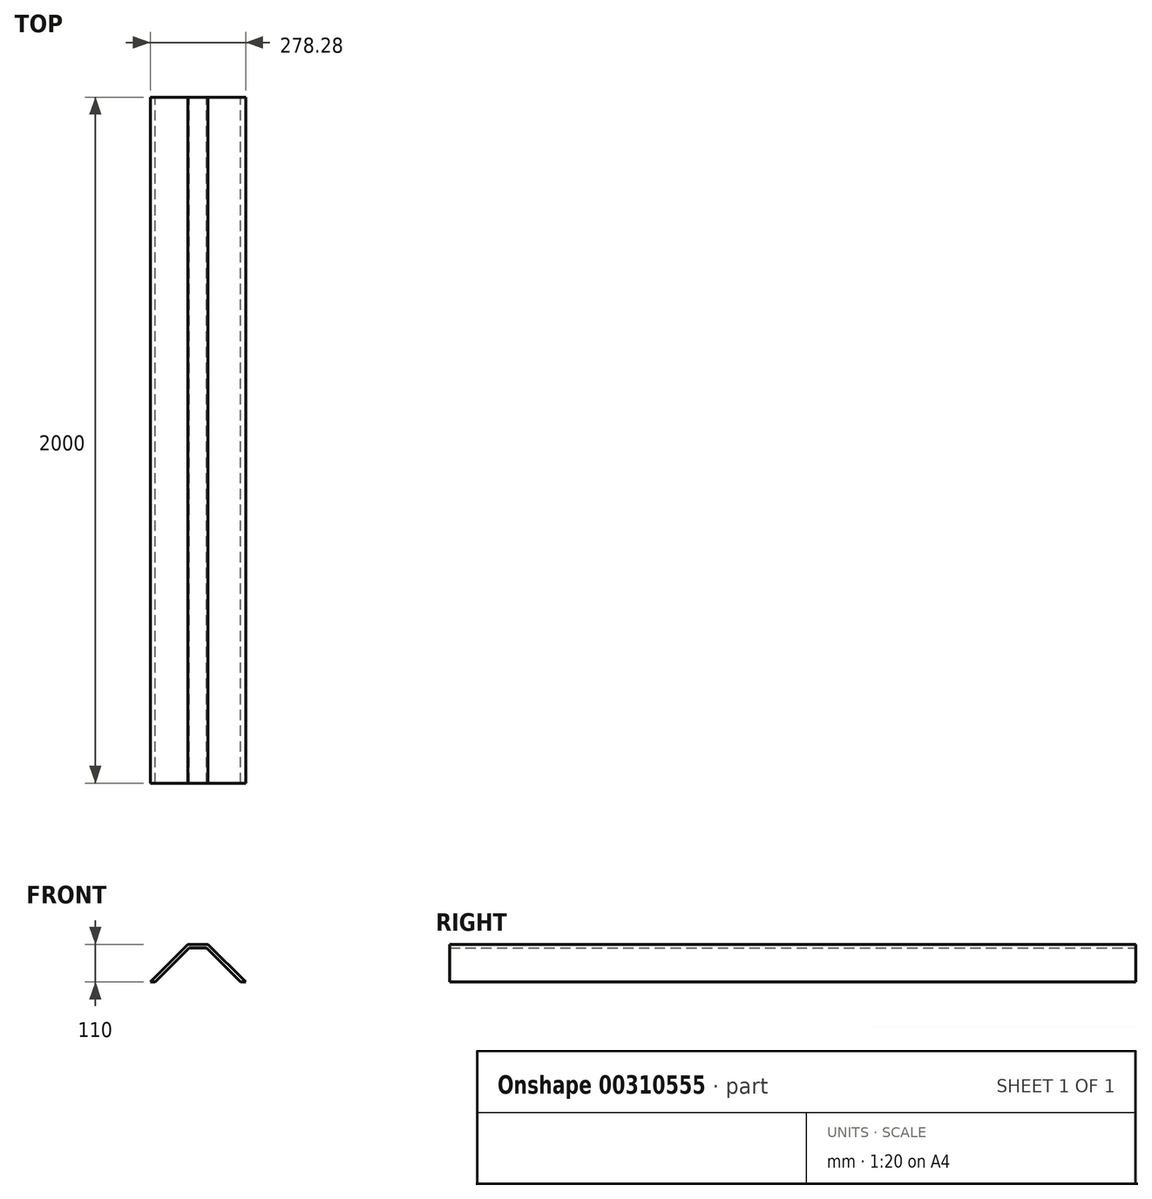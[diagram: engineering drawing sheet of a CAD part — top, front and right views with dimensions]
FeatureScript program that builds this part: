
annotation { "Feature Type Name" : "Feature", "Feature Type Description" : "" }
export const myFeature = defineFeature(function(context is Context, id is Id, definition is map)
    precondition{}
    {
        {
            var Q0;
            Q0=qCreatedBy(makeId("Front.planeOp"),FACE);
            var sketch = newSketch(context, id + "F0", { "sketchPlane" : qUnion([Q0])});
            skLineSegment(sketch, "E0", {"start": v(139.14, 0) * mm, "end": v(125, 0) * mm});
            skLineSegment(sketch, "E1", {"start": v(125, 0) * mm, "end": v(25, 100) * mm});
            skLineSegment(sketch, "E2", {"start": v(25, 100) * mm, "end": v(-25, 100) * mm});
            skLineSegment(sketch, "E3", {"start": v(-25, 100) * mm, "end": v(-125, 0) * mm});
            skLineSegment(sketch, "E4", {"start": v(-125, 0) * mm, "end": v(-139.14, 0) * mm});
            skLineSegment(sketch, "E5", {"start": v(-139.14, 0) * mm, "end": v(-29.14, 110) * mm});
            skLineSegment(sketch, "E6", {"start": v(-29.14, 110) * mm, "end": v(29.14, 110) * mm});
            skLineSegment(sketch, "E7", {"start": v(29.14, 110) * mm, "end": v(139.14, 0) * mm});
            skSolve(sketch);
        }
        {
            var Q0;
            Q0=qCreatedBy(makeId("Top.planeOp"),FACE);
            var sketch = newSketch(context, id + "F1", { "sketchPlane" : qUnion([Q0])});
            skLineSegment(sketch, "E8", {"start": v(0, 0) * mm, "end": v(0, 2000) * mm});
            skSolve(sketch);
        }
        {
            var Q0;
            Q0=makeQuery(id+"F0.imprint","IMPRINT",FACE,{"disambiguationData":[TD([[makeQuery(id+"F0.imprint","IMPRINT",EDGE,{"derivedFrom":sQuery(id+"F0.wireOp",EDGE,"E0")}),-1.0]])]});
            var Q1;
            Q1=sQuery(id+"F1.wireOp",EDGE,"E8");
            sweep(context, id + "F2", {"profiles" : qUnion([Q0]), "path" : qUnion([Q1])});
        }
    });
